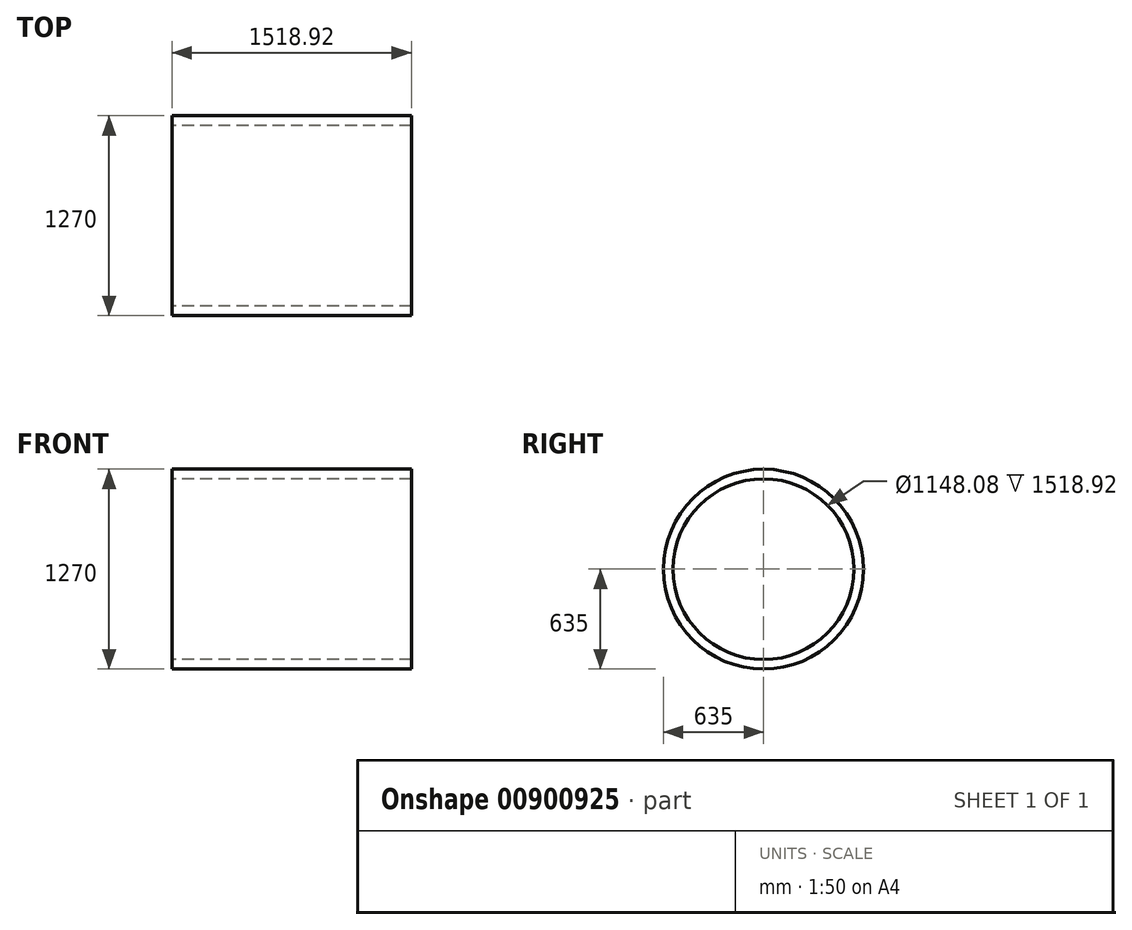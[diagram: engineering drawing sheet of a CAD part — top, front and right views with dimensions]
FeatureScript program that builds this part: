
annotation { "Feature Type Name" : "Feature", "Feature Type Description" : "" }
export const myFeature = defineFeature(function(context is Context, id is Id, definition is map)
    precondition{}
    {
        {
            var Q0;
            Q0=qCreatedBy(makeId("Right.planeOp"),FACE);
            var sketch = newSketch(context, id + "F0", { "sketchPlane" : qUnion([Q0])});
            skCircle(sketch, "E0", {"center": v(0, 0) * mm, "radius": 635 * mm});
            skCircle(sketch, "E1", {"center": v(0, 0) * mm, "radius": 574.04 * mm});
            skLineSegment(sketch, "E2", {"start": v(0, 0) * mm, "end": v(328.03, 568.17) * mm});
            skLineSegment(sketch, "E3", {"start": v(0, 0) * mm, "end": v(0, 877.7) * mm});
            skLineSegment(sketch, "E4", {"start": v(0, 0) * mm, "end": v(-364.4, -631.17) * mm});
            skLineSegment(sketch, "E5", {"start": v(0, 0) * mm, "end": v(-483.76, 483.76) * mm});
            skLineSegment(sketch, "E6", {"start": v(0, 0) * mm, "end": v(-484.48, -484.48) * mm});
            skLineSegment(sketch, "E7", {"start": v(0, 0) * mm, "end": v(487.47, -487.47) * mm});
            skLineSegment(sketch, "E8", {"start": v(0, 0) * mm, "end": v(470.65, 470.65) * mm});
            skLineSegment(sketch, "E9", {"start": v(-126.68, 622.24) * mm, "end": v(-126.68, 559.89) * mm});
            skLineSegment(sketch, "E10", {"start": v(127.32, 559.74) * mm, "end": v(127.32, 622.1) * mm});
            skLineSegment(sketch, "E11", {"start": v(378.92, 431.21) * mm, "end": v(422.1, 474.4) * mm});
            skLineSegment(sketch, "E12", {"start": v(433.08, 376.79) * mm, "end": v(478.52, 417.42) * mm});
            skLineSegment(sketch, "E13", {"start": v(435.94, -373.47) * mm, "end": v(480.98, -414.59) * mm});
            skLineSegment(sketch, "E14", {"start": v(376.82, -433.04) * mm, "end": v(419.54, -476.66) * mm});
            skLineSegment(sketch, "E15", {"start": v(-432.63, -377.3) * mm, "end": v(-475.83, -420.5) * mm});
            skLineSegment(sketch, "E16", {"start": v(-418.53, -477.55) * mm, "end": v(-377.9, -432.1) * mm});
            skLineSegment(sketch, "E17", {"start": v(-430.9, 379.27) * mm, "end": v(-471.8, 425) * mm});
            skLineSegment(sketch, "E18", {"start": v(-423.49, 473.16) * mm, "end": v(-380.3, 429.99) * mm});
            skSolve(sketch);
        }
        {
            var Q0;
            Q0=qSketchRegion(id+"F0",true);
            extrude(context, id + "F1", {"entities" : qUnion([Q0]), "depth" : 1518.92 * mm, "offsetDistance" : 25.4 * mm});
        }
    });
